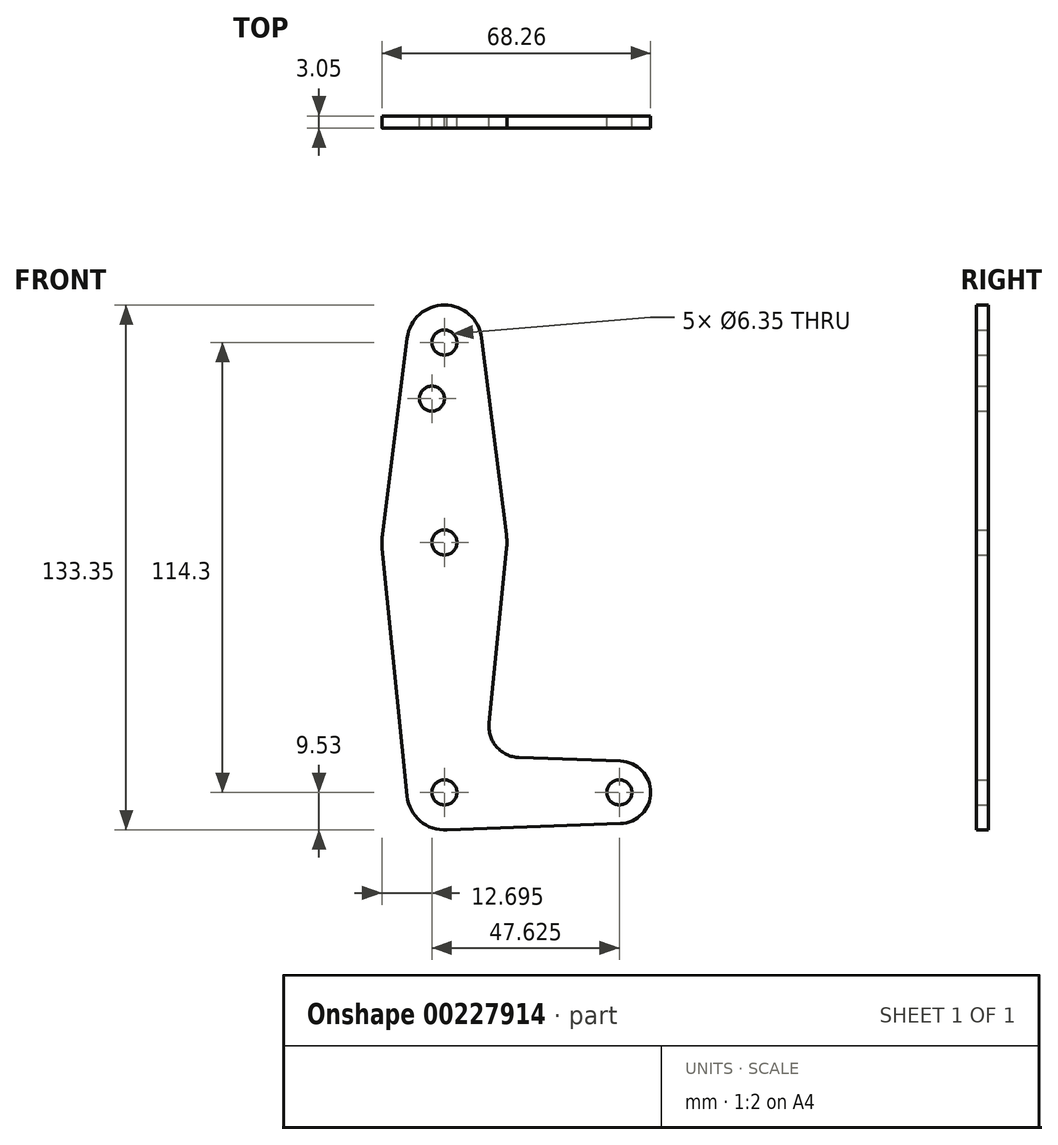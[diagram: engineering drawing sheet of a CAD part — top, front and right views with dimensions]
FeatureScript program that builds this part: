
annotation { "Feature Type Name" : "Feature", "Feature Type Description" : "" }
export const myFeature = defineFeature(function(context is Context, id is Id, definition is map)
    precondition{}
    {
        {
            var Q0;
            Q0=qCreatedBy(makeId("Front.planeOp"),FACE);
            var sketch = newSketch(context, id + "F0", { "sketchPlane" : qUnion([Q0])});
            skLineSegment(sketch, "E0", {"start": v(0, 50.8) * mm, "end": v(0, -63.5) * mm, "construction": true});
            skLineSegment(sketch, "E1", {"start": v(0, -63.5) * mm, "end": v(44.45, -63.5) * mm, "construction": true});
            skCircle(sketch, "E2", {"center": v(0, 50.8) * mm, "radius": 9.53 * mm});
            skCircle(sketch, "E3", {"center": v(0, 0) * mm, "radius": 15.88 * mm});
            skCircle(sketch, "E4", {"center": v(44.45, -63.5) * mm, "radius": 7.94 * mm});
            skLineSegment(sketch, "E5", {"start": v(-9.45, 52) * mm, "end": v(-15.75, 1.98) * mm});
            skLineSegment(sketch, "E6", {"start": v(9.45, 52) * mm, "end": v(15.75, 1.98) * mm});
            skCircle(sketch, "E7", {"center": v(-3.17, 36.53) * mm, "radius": 3.18 * mm});
            skCircle(sketch, "E8", {"center": v(0, 0) * mm, "radius": 3.18 * mm});
            skCircle(sketch, "E9", {"center": v(0, -63.5) * mm, "radius": 3.18 * mm});
            skCircle(sketch, "E10", {"center": v(44.45, -63.5) * mm, "radius": 3.18 * mm});
            skCircle(sketch, "E11", {"center": v(0, -63.5) * mm, "radius": 9.53 * mm});
            skLineSegment(sketch, "E12", {"start": v(-15.8, -1.59) * mm, "end": v(-9.48, -64.45) * mm});
            skLineSegment(sketch, "E13", {"start": v(15.8, -1.59) * mm, "end": v(11.34, -45.91) * mm});
            skLineSegment(sketch, "E14", {"start": v(18.97, -54.65) * mm, "end": v(44.73, -55.57) * mm});
            skLineSegment(sketch, "E15", {"start": v(0, -73.03) * mm, "end": v(44.73, -71.43) * mm});
            skCircle(sketch, "E16", {"center": v(0, 50.8) * mm, "radius": 3.18 * mm});
            skArc(sketch, "E17.filletArc", {"start": v(11.34, -45.91) * mm, "mid": v(13.26, -51.93) * mm, "end": v(18.97, -54.65) * mm});
            skSolve(sketch);
        }
        {
            var Q0;
            Q0 = qSketchRegion(id + "F0", true);
            extrude(context, id + "F1", {"entities" : qUnion([Q0]), "depth" : 3.05 * mm});
        }
    });
